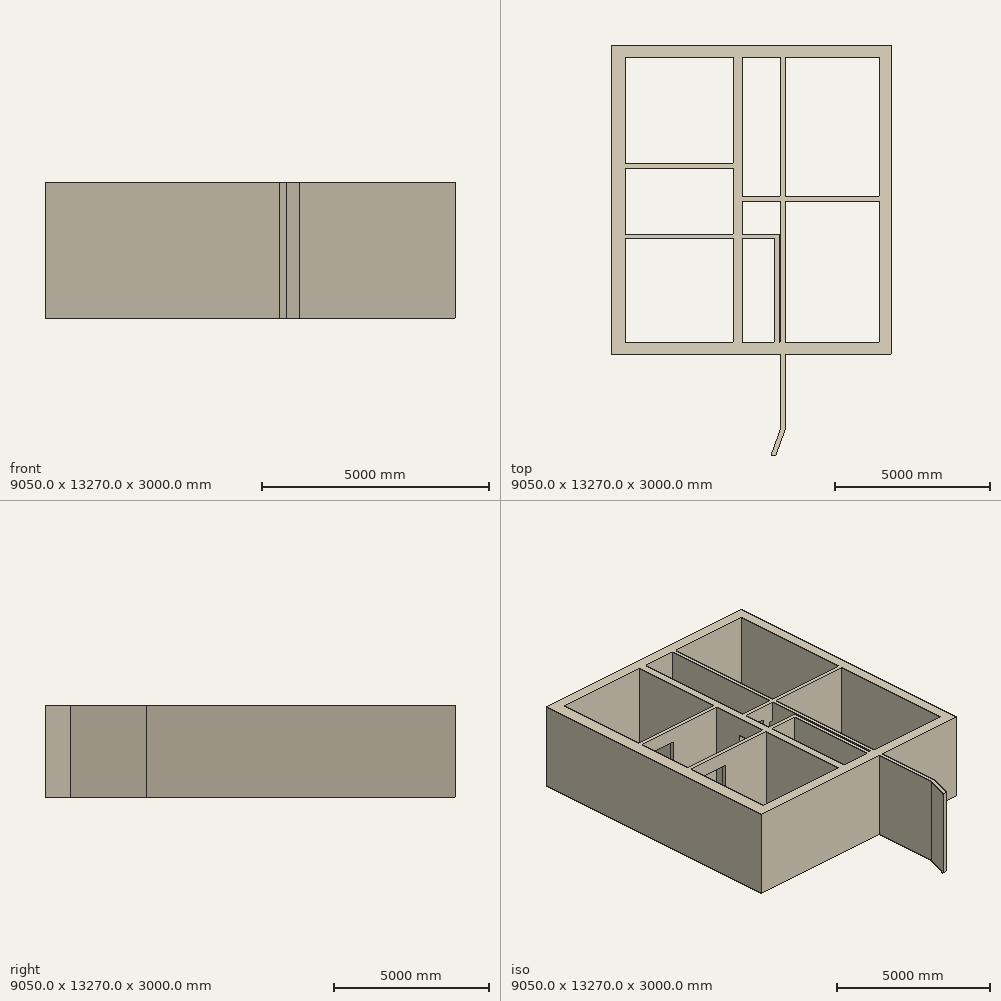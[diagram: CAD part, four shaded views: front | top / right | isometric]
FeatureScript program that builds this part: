
annotation { "Feature Type Name" : "Feature", "Feature Type Description" : "" }
export const myFeature = defineFeature(function(context is Context, id is Id, definition is map)
    precondition{}
    {
        {
            var Q0;
            Q0=qCreatedBy(makeId("Top.planeOp"),FACE);
            var sketch = newSketch(context, id + "F0", { "sketchPlane" : qUnion([Q0])});
            skLineSegment(sketch, "E0.bottom", {"start": v(-4439.04, 12738.42) * mm, "end": v(4610.96, 12738.42) * mm});
            skLineSegment(sketch, "E0.top", {"start": v(-4439.04, 2738.42) * mm, "end": v(4610.96, 2738.42) * mm});
            skLineSegment(sketch, "E0.right", {"start": v(4610.96, 12738.42) * mm, "end": v(4610.96, 2738.42) * mm});
            skLineSegment(sketch, "E1.left", {"start": v(-4439.04, 2738.42) * mm, "end": v(-4439.04, 12738.42) * mm});
            skLineSegment(sketch, "E2.bottom", {"start": v(-3989.04, 12358.42) * mm, "end": v(-489.04, 12358.42) * mm});
            skLineSegment(sketch, "E2.top", {"start": v(-3989.04, 8908.42) * mm, "end": v(-489.04, 8908.42) * mm});
            skLineSegment(sketch, "E2.left", {"start": v(-3989.04, 12358.42) * mm, "end": v(-3989.04, 8908.42) * mm});
            skLineSegment(sketch, "E2.right", {"start": v(-489.04, 12358.42) * mm, "end": v(-489.04, 8908.42) * mm});
            skLineSegment(sketch, "E3.bottom", {"start": v(-3989.04, 3118.42) * mm, "end": v(-489.04, 3118.42) * mm});
            skLineSegment(sketch, "E3.top", {"start": v(-3989.04, 6478.42) * mm, "end": v(-489.04, 6478.42) * mm});
            skLineSegment(sketch, "E3.left", {"start": v(-3989.04, 3118.42) * mm, "end": v(-3989.04, 6478.42) * mm});
            skLineSegment(sketch, "E3.right", {"start": v(-489.04, 3118.42) * mm, "end": v(-489.04, 6478.42) * mm});
            skLineSegment(sketch, "E4.bottom", {"start": v(-3989.04, 8768.42) * mm, "end": v(-489.04, 8768.42) * mm});
            skLineSegment(sketch, "E4.top", {"start": v(-3989.04, 6618.42) * mm, "end": v(-489.04, 6618.42) * mm});
            skLineSegment(sketch, "E4.left", {"start": v(-3989.04, 8768.42) * mm, "end": v(-3989.04, 6618.42) * mm});
            skLineSegment(sketch, "E4.right", {"start": v(-489.04, 8768.42) * mm, "end": v(-489.04, 6618.42) * mm});
            skLineSegment(sketch, "E5.bottom", {"start": v(-219.04, 12358.42) * mm, "end": v(4230.96, 12358.42) * mm});
            skLineSegment(sketch, "E5.top", {"start": v(-219.04, 7838.42) * mm, "end": v(4230.96, 7838.42) * mm});
            skLineSegment(sketch, "E5.left", {"start": v(-219.04, 12358.42) * mm, "end": v(-219.04, 7838.42) * mm});
            skLineSegment(sketch, "E5.right", {"start": v(4230.96, 12358.42) * mm, "end": v(4230.96, 7838.42) * mm});
            skLineSegment(sketch, "E6.bottom", {"start": v(-219.04, 7698.42) * mm, "end": v(4230.96, 7698.42) * mm});
            skLineSegment(sketch, "E6.top", {"start": v(-219.04, 3118.42) * mm, "end": v(4230.96, 3118.42) * mm});
            skLineSegment(sketch, "E6.left", {"start": v(-219.04, 7698.42) * mm, "end": v(-219.04, 3118.42) * mm});
            skLineSegment(sketch, "E6.right", {"start": v(4230.96, 7698.42) * mm, "end": v(4230.96, 3118.42) * mm});
            skSolve(sketch);
        }
        {
            var Q0;
            Q0=qSketchRegion(id+"F0",true);
            extrude(context, id + "F1", {"entities" : qUnion([Q0]), "depth" : 3000 * mm});
        }
        {
            var Q0;
            Q0=makeQuery(id+"F1.opExtrude","SWEPT_FACE",FACE,{"disambiguationData":[OSD([sQuery(id+"F0.wireOp",EDGE,"E4.bottom")])]});
            var sketch = newSketch(context, id + "F2", { "sketchPlane" : qUnion([Q0])});
            skLineSegment(sketch, "E7.bottom", {"start": v(-3489.04, 0) * mm, "end": v(-2489.04, 0) * mm});
            skLineSegment(sketch, "E7.top", {"start": v(-3489.04, 2500) * mm, "end": v(-2489.04, 2500) * mm});
            skLineSegment(sketch, "E7.left", {"start": v(-3489.04, 0) * mm, "end": v(-3489.04, 2500) * mm});
            skLineSegment(sketch, "E7.right", {"start": v(-2489.04, 0) * mm, "end": v(-2489.04, 2500) * mm});
            skSolve(sketch);
        }
        {
            var Q0;
            Q0=qSketchRegion(id+"F2",true);
            extrude(context, id + "F3", {"entities" : qUnion([Q0]), "operationType" : NewBodyOperationType.REMOVE, "endBound" : BoundingType.UP_TO_NEXT, "oppositeDirection" : true, "depth" : 25 * mm});
        }
        {
            var Q0;
            Q0=makeQuery(id+"F1.opExtrude","SWEPT_FACE",FACE,{"disambiguationData":[OSD([sQuery(id+"F0.wireOp",EDGE,"E4.top")])]});
            var sketch = newSketch(context, id + "F4", { "sketchPlane" : qUnion([Q0])});
            skLineSegment(sketch, "E8.bottom", {"start": v(2389.04, 0) * mm, "end": v(3389.04, 0) * mm});
            skLineSegment(sketch, "E8.top", {"start": v(2389.04, 2500) * mm, "end": v(3389.04, 2500) * mm});
            skLineSegment(sketch, "E8.left", {"start": v(2389.04, 0) * mm, "end": v(2389.04, 2500) * mm});
            skLineSegment(sketch, "E8.right", {"start": v(3389.04, 0) * mm, "end": v(3389.04, 2500) * mm});
            skSolve(sketch);
        }
        {
            var Q0;
            Q0=qSketchRegion(id+"F4",true);
            extrude(context, id + "F5", {"entities" : qUnion([Q0]), "operationType" : NewBodyOperationType.REMOVE, "endBound" : BoundingType.UP_TO_NEXT, "oppositeDirection" : true, "depth" : 25 * mm});
        }
        {
            var Q0;
            Q0=makeQuery(id+"F1.opExtrude","SWEPT_FACE",FACE,{"disambiguationData":[OSD([sQuery(id+"F0.wireOp",EDGE,"E5.top")])]});
            var sketch = newSketch(context, id + "F6", { "sketchPlane" : qUnion([Q0])});
            skLineSegment(sketch, "E9.bottom", {"start": v(-1880.96, 0) * mm, "end": v(-880.96, 0) * mm});
            skLineSegment(sketch, "E9.top", {"start": v(-1880.96, 2296.22) * mm, "end": v(-880.96, 2296.22) * mm});
            skLineSegment(sketch, "E9.left", {"start": v(-1880.96, 0) * mm, "end": v(-1880.96, 2296.22) * mm});
            skLineSegment(sketch, "E9.right", {"start": v(-880.96, 0) * mm, "end": v(-880.96, 2296.22) * mm});
            skSolve(sketch);
        }
        {
            var Q0;
            Q0=qSketchRegion(id+"F6",true);
            extrude(context, id + "F7", {"entities" : qUnion([Q0]), "operationType" : NewBodyOperationType.REMOVE, "endBound" : BoundingType.UP_TO_NEXT, "oppositeDirection" : true, "depth" : 25 * mm});
        }
        {
            var Q0;
            Q0=makeQuery(id+"F1.opExtrude","SWEPT_FACE",FACE,{"disambiguationData":[OSD([sQuery(id+"F0.wireOp",EDGE,"E4.right")])]});
            var sketch = newSketch(context, id + "F8", { "sketchPlane" : qUnion([Q0])});
            skLineSegment(sketch, "E10.bottom", {"start": v(-7698.42, 0) * mm, "end": v(-6898.42, 0) * mm});
            skLineSegment(sketch, "E10.top", {"start": v(-7698.42, 2353.11) * mm, "end": v(-6898.42, 2353.11) * mm});
            skLineSegment(sketch, "E10.left", {"start": v(-7698.42, 0) * mm, "end": v(-7698.42, 2353.11) * mm});
            skLineSegment(sketch, "E10.right", {"start": v(-6898.42, 0) * mm, "end": v(-6898.42, 2353.11) * mm});
            skSolve(sketch);
        }
        {
            var Q0;
            Q0=qSketchRegion(id+"F8",true);
            extrude(context, id + "F9", {"entities" : qUnion([Q0]), "operationType" : NewBodyOperationType.REMOVE, "endBound" : BoundingType.UP_TO_NEXT, "oppositeDirection" : true, "depth" : 25 * mm});
        }
        {
            var Q0;
            Q0=makeQuery(id+"F9.boolean.opBoolean","MERGE",FACE,{"derivedFrom":[makeQuery(id+"F1.opExtrude","SWEPT_FACE",FACE,{"disambiguationData":[OSD([sQuery(id+"F0.wireOp",EDGE,"E6.bottom")])]}),makeQuery(id+"F9.opExtrude","SWEPT_FACE",FACE,{"disambiguationData":[OSD([sQuery(id+"F8.wireOp",EDGE,"E10.left")])]})]});
            var sketch = newSketch(context, id + "F10", { "sketchPlane" : qUnion([Q0])});
            skLineSegment(sketch, "E11.bottom", {"start": v(580.96, 0) * mm, "end": v(-19.04, 0) * mm});
            skLineSegment(sketch, "E11.top", {"start": v(580.96, 2500) * mm, "end": v(-19.04, 2500) * mm});
            skLineSegment(sketch, "E11.left", {"start": v(580.96, 0) * mm, "end": v(580.96, 2500) * mm});
            skLineSegment(sketch, "E11.right", {"start": v(-19.04, 0) * mm, "end": v(-19.04, 2500) * mm});
            skSolve(sketch);
        }
        {
            var Q0;
            Q0=qSketchRegion(id+"F10",true);
            extrude(context, id + "F11", {"entities" : qUnion([Q0]), "operationType" : NewBodyOperationType.REMOVE, "endBound" : BoundingType.UP_TO_NEXT, "oppositeDirection" : true, "depth" : 25 * mm});
        }
        {
            var Q0;
            {var subQ0=sQuery(id+"F0.wireOp",EDGE,"E3.bottom");var subQ1=sQuery(id+"F0.wireOp",EDGE,"E6.right");var subQ2=sQuery(id+"F0.wireOp",EDGE,"E6.left");var subQ3=sQuery(id+"F0.wireOp",EDGE,"E6.top");var subQ4=sQuery(id+"F0.wireOp",EDGE,"E6.bottom");var subQ5=sQuery(id+"F0.wireOp",EDGE,"E5.right");var subQ6=sQuery(id+"F0.wireOp",EDGE,"E5.left");var subQ7=sQuery(id+"F0.wireOp",EDGE,"E5.top");var subQ8=sQuery(id+"F0.wireOp",EDGE,"E5.bottom");var subQ9=sQuery(id+"F0.wireOp",EDGE,"E4.left");var subQ10=sQuery(id+"F0.wireOp",EDGE,"E4.top");var subQ11=sQuery(id+"F0.wireOp",EDGE,"E4.bottom");var subQ12=sQuery(id+"F0.wireOp",EDGE,"E3.right");var subQ13=sQuery(id+"F0.wireOp",EDGE,"E3.left");var subQ14=sQuery(id+"F0.wireOp",EDGE,"E0.bottom");var subQ15=sQuery(id+"F0.wireOp",EDGE,"E3.top");var subQ16=sQuery(id+"F0.wireOp",EDGE,"DndnOUUW-Cvbm-U9KY-F6qv-hL9b6goUNXXM.left");var subQ17=sQuery(id+"F0.wireOp",EDGE,"DndnOUUW-Cvbm-U9KY-F6qv-hL9b6goUNXXM.top");var subQ18=sQuery(id+"F0.wireOp",EDGE,"DndnOUUW-Cvbm-U9KY-F6qv-hL9b6goUNXXM.bottom");var subQ19=sQuery(id+"F0.wireOp",EDGE,"CQFG8qXA-LsU4-KCIn-jFd3-hTCcTj04gsu6.right");var subQ20=sQuery(id+"F0.wireOp",EDGE,"CQFG8qXA-LsU4-KCIn-jFd3-hTCcTj04gsu6.top");var subQ21=sQuery(id+"F0.wireOp",EDGE,"DndnOUUW-Cvbm-U9KY-F6qv-hL9b6goUNXXM.right");var subQ22=sQuery(id+"F0.wireOp",EDGE,"E2.right");var subQ23=sQuery(id+"F0.wireOp",EDGE,"E0.right");var subQ24=sQuery(id+"F0.wireOp",EDGE,"E0.top");var subQ25=sQuery(id+"F0.wireOp",EDGE,"E0.left");var subQ26=sQuery(id+"F0.wireOp",EDGE,"jH5GhPCs-LNaf-BreG-eQWe-3JrbFfGwmy1A.bottom");var subQ27=sQuery(id+"F0.wireOp",EDGE,"jH5GhPCs-LNaf-BreG-eQWe-3JrbFfGwmy1A.top");var subQ28=sQuery(id+"F0.wireOp",EDGE,"jH5GhPCs-LNaf-BreG-eQWe-3JrbFfGwmy1A.left");var subQ29=sQuery(id+"F0.wireOp",EDGE,"jH5GhPCs-LNaf-BreG-eQWe-3JrbFfGwmy1A.right");var subQ30=sQuery(id+"F0.wireOp",EDGE,"E1.bottom");var subQ31=sQuery(id+"F0.wireOp",EDGE,"E1.top");var subQ32=sQuery(id+"F0.wireOp",EDGE,"E1.left");var subQ33=sQuery(id+"F0.wireOp",EDGE,"E1.right");var subQ34=sQuery(id+"F0.wireOp",EDGE,"E2.bottom");var subQ35=sQuery(id+"F0.wireOp",EDGE,"E2.top");var subQ36=sQuery(id+"F0.wireOp",EDGE,"E2.left");Q0=makeQuery(id+"FWmasmGtrgQR82j_1.boolean.opBoolean","SPLIT",FACE,{"disambiguationData":[TD([makeQuery(id+"F1.opExtrude","SWEPT_FACE",FACE,{"disambiguationData":[OSD([subQ14])]})])],"derivedFrom":makeQuery(id+"F1.opExtrude","CAP_FACE",FACE,{"disambiguationData":[OSD([subQ14,subQ24,subQ25,subQ23,subQ20,subQ19,subQ18,subQ17,subQ16,subQ21,subQ26,subQ27,subQ28,subQ29,subQ30,subQ31,subQ32,subQ33,subQ34,subQ35,subQ36,subQ22,subQ0,subQ15,subQ13,subQ12,subQ11,subQ10,subQ9,sQuery(id+"F0.wireOp",EDGE,"E4.right"),subQ8,subQ7,subQ6,subQ5,subQ4,subQ3,subQ2,subQ1])],"isStart":true})});}
            var sketch = newSketch(context, id + "F12", { "sketchPlane" : qUnion([Q0])});
            skLineSegment(sketch, "E12.top", {"start": v(1170.96, -12358.42) * mm, "end": v(1030.96, -12358.42) * mm});
            skLineSegment(sketch, "E12.left", {"start": v(1170.96, -271.58) * mm, "end": v(1170.96, -12358.42) * mm});
            skLineSegment(sketch, "E13", {"start": v(878.64, 531.58) * mm, "end": v(719, 531.58) * mm});
            skLineSegment(sketch, "E14", {"start": v(719, 531.58) * mm, "end": v(1030.96, -325.5) * mm});
            skLineSegment(sketch, "E15", {"start": v(1170.96, -271.58) * mm, "end": v(878.64, 531.58) * mm});
            skLineSegment(sketch, "E16.trimOffspring", {"start": v(1030.96, -325.5) * mm, "end": v(1030.96, -12358.42) * mm});
            skSolve(sketch);
        }
        {
            var Q0;
            Q0=qSketchRegion(id+"F12",true);
            var Q1;
            Q1=makeQuery(id+"F1.opExtrude","CAP_FACE",FACE,{"disambiguationData":[OSD([sQuery(id+"F0.wireOp",EDGE,"E0.bottom"),sQuery(id+"F0.wireOp",EDGE,"E0.top"),sQuery(id+"F0.wireOp",EDGE,"E0.left"),sQuery(id+"F0.wireOp",EDGE,"E0.right"),sQuery(id+"F0.wireOp",EDGE,"CQFG8qXA-LsU4-KCIn-jFd3-hTCcTj04gsu6.top"),sQuery(id+"F0.wireOp",EDGE,"CQFG8qXA-LsU4-KCIn-jFd3-hTCcTj04gsu6.right"),sQuery(id+"F0.wireOp",EDGE,"DndnOUUW-Cvbm-U9KY-F6qv-hL9b6goUNXXM.bottom"),sQuery(id+"F0.wireOp",EDGE,"DndnOUUW-Cvbm-U9KY-F6qv-hL9b6goUNXXM.top"),sQuery(id+"F0.wireOp",EDGE,"DndnOUUW-Cvbm-U9KY-F6qv-hL9b6goUNXXM.left"),sQuery(id+"F0.wireOp",EDGE,"DndnOUUW-Cvbm-U9KY-F6qv-hL9b6goUNXXM.right"),sQuery(id+"F0.wireOp",EDGE,"jH5GhPCs-LNaf-BreG-eQWe-3JrbFfGwmy1A.bottom"),sQuery(id+"F0.wireOp",EDGE,"jH5GhPCs-LNaf-BreG-eQWe-3JrbFfGwmy1A.top"),sQuery(id+"F0.wireOp",EDGE,"jH5GhPCs-LNaf-BreG-eQWe-3JrbFfGwmy1A.left"),sQuery(id+"F0.wireOp",EDGE,"jH5GhPCs-LNaf-BreG-eQWe-3JrbFfGwmy1A.right"),sQuery(id+"F0.wireOp",EDGE,"E1.bottom"),sQuery(id+"F0.wireOp",EDGE,"E1.top"),sQuery(id+"F0.wireOp",EDGE,"E1.left"),sQuery(id+"F0.wireOp",EDGE,"E1.right"),sQuery(id+"F0.wireOp",EDGE,"E2.bottom"),sQuery(id+"F0.wireOp",EDGE,"E2.top"),sQuery(id+"F0.wireOp",EDGE,"E2.left"),sQuery(id+"F0.wireOp",EDGE,"E2.right"),sQuery(id+"F0.wireOp",EDGE,"E3.bottom"),sQuery(id+"F0.wireOp",EDGE,"E3.top"),sQuery(id+"F0.wireOp",EDGE,"E3.left"),sQuery(id+"F0.wireOp",EDGE,"E3.right"),sQuery(id+"F0.wireOp",EDGE,"E4.bottom"),sQuery(id+"F0.wireOp",EDGE,"E4.top"),sQuery(id+"F0.wireOp",EDGE,"E4.left"),sQuery(id+"F0.wireOp",EDGE,"E4.right"),sQuery(id+"F0.wireOp",EDGE,"E5.bottom"),sQuery(id+"F0.wireOp",EDGE,"E5.top"),sQuery(id+"F0.wireOp",EDGE,"E5.left"),sQuery(id+"F0.wireOp",EDGE,"E5.right"),sQuery(id+"F0.wireOp",EDGE,"E6.bottom"),sQuery(id+"F0.wireOp",EDGE,"E6.top"),sQuery(id+"F0.wireOp",EDGE,"E6.left"),sQuery(id+"F0.wireOp",EDGE,"E6.right")])],"isStart":false});
            extrude(context, id + "F13", {"entities" : qUnion([Q0]), "operationType" : NewBodyOperationType.ADD, "endBound" : BoundingType.UP_TO_SURFACE, "oppositeDirection" : true, "endBoundEntityFace" : qUnion([Q1]), "depth" : 25 * mm});
        }
        {
            var Q0;
            {var subQ0=sQuery(id+"F0.wireOp",EDGE,"E4.right");var subQ1=makeQuery(id+"F1.opExtrude","SWEPT_FACE",FACE,{"disambiguationData":[OSD([subQ0])]});var subQ3=sQuery(id+"F0.wireOp",EDGE,"E4.top");var subQ5=sQuery(id+"F0.wireOp",EDGE,"E3.right");var subQ7=sQuery(id+"F0.wireOp",EDGE,"E6.left");var subQ9=sQuery(id+"F0.wireOp",EDGE,"E3.top");var subQ10=makeQuery(id+"F1.opExtrude","SWEPT_FACE",FACE,{"disambiguationData":[OSD([subQ9])]});var subQ12=sQuery(id+"F0.wireOp",EDGE,"E5.top");var subQ13=sQuery(id+"F0.wireOp",EDGE,"E4.bottom");var subQ14=sQuery(id+"F0.wireOp",EDGE,"E2.top");var subQ15=sQuery(id+"F0.wireOp",EDGE,"E5.left");var subQ16=sQuery(id+"F0.wireOp",EDGE,"E2.right");var subQ17=sQuery(id+"F0.wireOp",EDGE,"E6.bottom");Q0=makeQuery(id+"F9.boolean.opBoolean","SPLIT",FACE,{"disambiguationData":[TD([subQ10])],"derivedFrom":makeQuery(id+"FWmasmGtrgQR82j_1.boolean.opBoolean","SPLIT",FACE,{"disambiguationData":[TD([subQ1])],"derivedFrom":makeQuery(id+"F1.opExtrude","CAP_FACE",FACE,{"disambiguationData":[OSD([sQuery(id+"F0.wireOp",EDGE,"E0.bottom"),sQuery(id+"F0.wireOp",EDGE,"E0.top"),sQuery(id+"F0.wireOp",EDGE,"E0.left"),sQuery(id+"F0.wireOp",EDGE,"E0.right"),sQuery(id+"F0.wireOp",EDGE,"CQFG8qXA-LsU4-KCIn-jFd3-hTCcTj04gsu6.top"),sQuery(id+"F0.wireOp",EDGE,"CQFG8qXA-LsU4-KCIn-jFd3-hTCcTj04gsu6.right"),sQuery(id+"F0.wireOp",EDGE,"DndnOUUW-Cvbm-U9KY-F6qv-hL9b6goUNXXM.bottom"),sQuery(id+"F0.wireOp",EDGE,"DndnOUUW-Cvbm-U9KY-F6qv-hL9b6goUNXXM.top"),sQuery(id+"F0.wireOp",EDGE,"DndnOUUW-Cvbm-U9KY-F6qv-hL9b6goUNXXM.left"),sQuery(id+"F0.wireOp",EDGE,"DndnOUUW-Cvbm-U9KY-F6qv-hL9b6goUNXXM.right"),sQuery(id+"F0.wireOp",EDGE,"jH5GhPCs-LNaf-BreG-eQWe-3JrbFfGwmy1A.bottom"),sQuery(id+"F0.wireOp",EDGE,"jH5GhPCs-LNaf-BreG-eQWe-3JrbFfGwmy1A.top"),sQuery(id+"F0.wireOp",EDGE,"jH5GhPCs-LNaf-BreG-eQWe-3JrbFfGwmy1A.left"),sQuery(id+"F0.wireOp",EDGE,"jH5GhPCs-LNaf-BreG-eQWe-3JrbFfGwmy1A.right"),sQuery(id+"F0.wireOp",EDGE,"E1.bottom"),sQuery(id+"F0.wireOp",EDGE,"E1.top"),sQuery(id+"F0.wireOp",EDGE,"E1.left"),sQuery(id+"F0.wireOp",EDGE,"E1.right"),sQuery(id+"F0.wireOp",EDGE,"E2.bottom"),subQ14,sQuery(id+"F0.wireOp",EDGE,"E2.left"),subQ16,sQuery(id+"F0.wireOp",EDGE,"E3.bottom"),subQ9,sQuery(id+"F0.wireOp",EDGE,"E3.left"),subQ5,subQ13,subQ3,sQuery(id+"F0.wireOp",EDGE,"E4.left"),subQ0,sQuery(id+"F0.wireOp",EDGE,"E5.bottom"),subQ12,subQ15,sQuery(id+"F0.wireOp",EDGE,"E5.right"),subQ17,sQuery(id+"F0.wireOp",EDGE,"E6.top"),subQ7,sQuery(id+"F0.wireOp",EDGE,"E6.right")])],"isStart":true})})});}
            var sketch = newSketch(context, id + "F14", { "sketchPlane" : qUnion([Q0])});
            skPoint(sketch, "E17.oppositeSnap0", {"position": v(-1439.04, -6618.42) * mm});
            skLineSegment(sketch, "E17.bottom", {"start": v(-219.04, -6478.42) * mm, "end": v(840.96, -6478.42) * mm});
            skLineSegment(sketch, "E17.top", {"start": v(-219.04, -6618.42) * mm, "end": v(980.96, -6618.42) * mm});
            skLineSegment(sketch, "E17.left", {"start": v(-219.04, -6478.42) * mm, "end": v(-219.04, -6618.42) * mm});
            skLineSegment(sketch, "E18.top", {"start": v(980.96, -3118.42) * mm, "end": v(840.96, -3118.42) * mm});
            skLineSegment(sketch, "E18.left", {"start": v(980.96, -6478.42) * mm, "end": v(980.96, -3118.42) * mm});
            skLineSegment(sketch, "E18.right", {"start": v(840.96, -6478.42) * mm, "end": v(840.96, -3118.42) * mm});
            skLineSegment(sketch, "E19", {"start": v(980.96, -6478.42) * mm, "end": v(980.96, -6618.42) * mm});
            skSolve(sketch);
        }
        {
            var Q0;
            Q0=qSketchRegion(id+"F14",true);
            var Q1;
            {var subQ0=sQuery(id+"F0.wireOp",EDGE,"E6.right");var subQ1=sQuery(id+"F0.wireOp",EDGE,"E6.left");var subQ2=sQuery(id+"F0.wireOp",EDGE,"E6.top");var subQ3=sQuery(id+"F0.wireOp",EDGE,"E6.bottom");var subQ4=sQuery(id+"F0.wireOp",EDGE,"E5.right");var subQ5=sQuery(id+"F0.wireOp",EDGE,"E5.left");var subQ6=sQuery(id+"F0.wireOp",EDGE,"E5.top");var subQ7=sQuery(id+"F0.wireOp",EDGE,"E5.bottom");var subQ8=sQuery(id+"F0.wireOp",EDGE,"E4.right");var subQ9=sQuery(id+"F0.wireOp",EDGE,"E4.left");var subQ10=sQuery(id+"F0.wireOp",EDGE,"E4.top");var subQ11=sQuery(id+"F0.wireOp",EDGE,"E4.bottom");var subQ12=sQuery(id+"F0.wireOp",EDGE,"E3.right");var subQ13=sQuery(id+"F0.wireOp",EDGE,"E3.left");var subQ14=sQuery(id+"F0.wireOp",EDGE,"E3.top");var subQ15=sQuery(id+"F0.wireOp",EDGE,"E3.bottom");var subQ16=sQuery(id+"F0.wireOp",EDGE,"E2.right");var subQ17=sQuery(id+"F0.wireOp",EDGE,"E2.left");var subQ18=sQuery(id+"F0.wireOp",EDGE,"E2.top");var subQ19=sQuery(id+"F0.wireOp",EDGE,"E2.bottom");var subQ20=sQuery(id+"F0.wireOp",EDGE,"E1.right");var subQ21=sQuery(id+"F0.wireOp",EDGE,"E1.left");var subQ22=sQuery(id+"F0.wireOp",EDGE,"E1.top");var subQ23=sQuery(id+"F0.wireOp",EDGE,"E1.bottom");var subQ24=sQuery(id+"F0.wireOp",EDGE,"jH5GhPCs-LNaf-BreG-eQWe-3JrbFfGwmy1A.right");var subQ25=sQuery(id+"F0.wireOp",EDGE,"jH5GhPCs-LNaf-BreG-eQWe-3JrbFfGwmy1A.left");var subQ26=sQuery(id+"F0.wireOp",EDGE,"jH5GhPCs-LNaf-BreG-eQWe-3JrbFfGwmy1A.top");var subQ27=sQuery(id+"F0.wireOp",EDGE,"jH5GhPCs-LNaf-BreG-eQWe-3JrbFfGwmy1A.bottom");var subQ28=sQuery(id+"F0.wireOp",EDGE,"DndnOUUW-Cvbm-U9KY-F6qv-hL9b6goUNXXM.right");var subQ29=sQuery(id+"F0.wireOp",EDGE,"DndnOUUW-Cvbm-U9KY-F6qv-hL9b6goUNXXM.left");var subQ30=sQuery(id+"F0.wireOp",EDGE,"DndnOUUW-Cvbm-U9KY-F6qv-hL9b6goUNXXM.top");var subQ31=sQuery(id+"F0.wireOp",EDGE,"DndnOUUW-Cvbm-U9KY-F6qv-hL9b6goUNXXM.bottom");var subQ32=sQuery(id+"F0.wireOp",EDGE,"CQFG8qXA-LsU4-KCIn-jFd3-hTCcTj04gsu6.right");var subQ33=sQuery(id+"F0.wireOp",EDGE,"CQFG8qXA-LsU4-KCIn-jFd3-hTCcTj04gsu6.top");var subQ34=sQuery(id+"F0.wireOp",EDGE,"E0.right");var subQ35=sQuery(id+"F0.wireOp",EDGE,"E0.left");var subQ36=sQuery(id+"F0.wireOp",EDGE,"E0.top");var subQ37=sQuery(id+"F0.wireOp",EDGE,"E0.bottom");Q1=makeQuery(id+"F13.boolean.opBoolean","MERGE",FACE,{"derivedFrom":[makeQuery(id+"F1.opExtrude","CAP_FACE",FACE,{"disambiguationData":[OSD([subQ37,subQ36,subQ35,subQ34,subQ33,subQ32,subQ31,subQ30,subQ29,subQ28,subQ27,subQ26,subQ25,subQ24,subQ23,subQ22,subQ21,subQ20,subQ19,subQ18,subQ17,subQ16,subQ15,subQ14,subQ13,subQ12,subQ11,subQ10,subQ9,subQ8,subQ7,subQ6,subQ5,subQ4,subQ3,subQ2,subQ1,subQ0])],"isStart":false}),makeQuery(id+"F13.opExtrude","CAP_FACE",FACE,{"disambiguationData":[OSD([subQ37,subQ36,subQ35,subQ34,subQ33,subQ32,subQ31,subQ30,subQ29,subQ28,subQ27,subQ26,subQ25,subQ24,subQ23,subQ22,subQ21,subQ20,subQ19,subQ18,subQ17,subQ16,subQ15,subQ14,subQ13,subQ12,subQ11,subQ10,subQ9,subQ8,subQ7,subQ6,subQ5,subQ4,subQ3,subQ2,subQ1,subQ0])],"isStart":false})]});}
            extrude(context, id + "F15", {"entities" : qUnion([Q0]), "operationType" : NewBodyOperationType.ADD, "endBound" : BoundingType.UP_TO_SURFACE, "oppositeDirection" : true, "endBoundEntityFace" : qUnion([Q1]), "depth" : 25 * mm, "offsetDistance" : 25 * mm});
        }
    });
